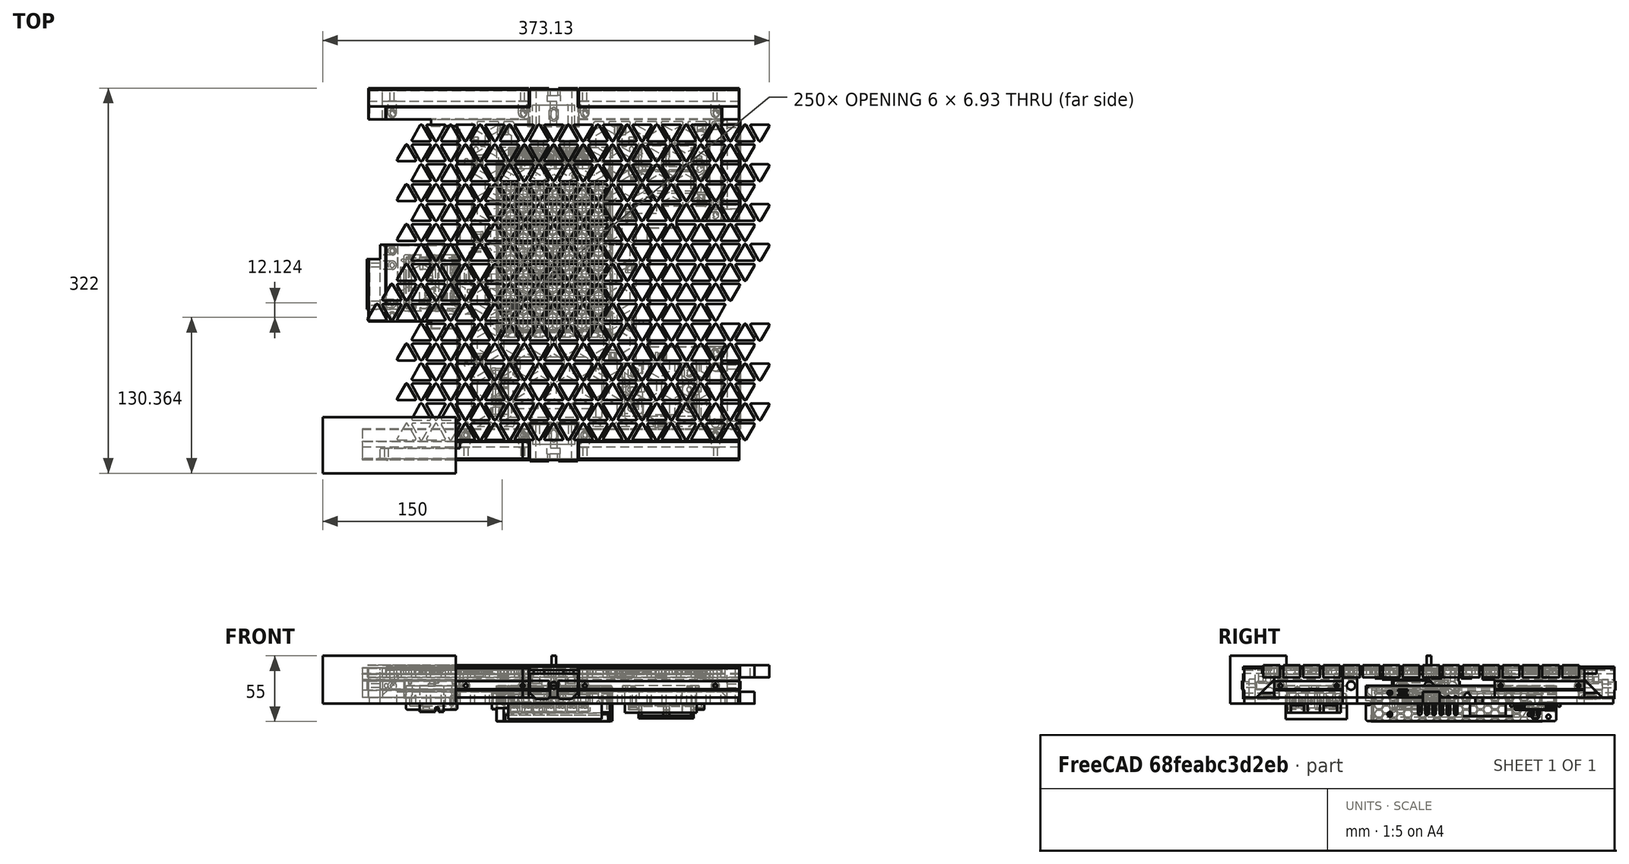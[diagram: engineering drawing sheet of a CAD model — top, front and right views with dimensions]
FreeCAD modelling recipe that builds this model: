
FCSTD DOCUMENT  (FreeCAD 0.19R24291 (Git))
Label: bottom-panel
License: Other
LicenseURL: GPL3
objects: Part::Feature×117, Part::Box×54, Part::MultiFuse×41, Part::Cut×29, Part::Cylinder×17, Part::Chamfer×14, Part::Fillet×5, Part::Extrusion×3, Mesh::Feature×1, Part::MultiCommon×1, Part::Refine×1
note: 282 computed .brp shape members not serialized (recipe doc carries the construction recipe); baked Part::Feature solids carry a one-line shape summary decoded from their .brp

FEATURE [Part::Box] Box  label="Cube"
  AttacherType = Attacher::AttachEngine3D
  Height = 3
  Length = 310
  Placement = pos=(-155,-155,28) rot=(0,0,1;0rad)
  Width = 310
FEATURE [Part::Box] Box002  label="Cube001"
  AttacherType = Attacher::AttachEngine3D
  Height = 10
  Length = 74.5
  Placement = pos=(80.5,-72,24) rot=(0,0,1;0rad)
  Width = 117
FEATURE [Part::Box] Box003  label="Cube002"
  AttacherType = Attacher::AttachEngine3D
  Height = 10
  Length = 74.5
  Placement = pos=(-155,-156,24) rot=(0,0,1;0rad)
  Width = 117
FEATURE [Part::Box] Box004  label="Cube003"
  AttacherType = Attacher::AttachEngine3D
  Height = 10
  Length = 74.5
  Placement = pos=(-155,13,24) rot=(0,0,1;0rad)
  Width = 117
FEATURE [Part::Box] Box005  label="Cube004"
  AttacherType = Attacher::AttachEngine3D
  Height = 3
  Length = 22
  Placement = pos=(-102.5,-45,28) rot=(0,0,1;0rad)
  Width = 6
FEATURE [Part::Box] Box006  label="Cube005"
  AttacherType = Attacher::AttachEngine3D
  Height = 3
  Length = 22
  Placement = pos=(80.5,39,28) rot=(0,0,1;0rad)
  Width = 6
FEATURE [Part::Box] Box007  label="Cube006"
  AttacherType = Attacher::AttachEngine3D
  Height = 3
  Length = 22
  Placement = pos=(-102.5,124,28) rot=(0,0,1;0rad)
  Width = 6
FEATURE [Part::Box] Box008  label="Cube007"
  AttacherType = Attacher::AttachEngine3D
  Height = 3
  Length = 64.5
  Placement = pos=(-145,-155,28) rot=(0,0,1;0rad)
  Width = 10
FEATURE [Part::Box] Box009  label="Cube008"
  AttacherType = Attacher::AttachEngine3D
  Height = 3
  Length = 64.5
  Placement = pos=(80.5,-72,28) rot=(0,0,1;0rad)
  Width = 12
FEATURE [Part::Box] Box010  label="Cube009"
  AttacherType = Attacher::AttachEngine3D
  Height = 3
  Length = 64.5
  Placement = pos=(-145,13,28) rot=(0,0,1;0rad)
  Width = 12
FEATURE [Part::Feature] Fusion006002011004053036004001028003005003001_cs001  label="base-plate-profile001"
  Placement = pos=(0,0,-29.5) rot=(0,0,1;0rad)
  shape: bbox 308 x 308 x 4e-07 mm, 0 faces, 0 solids (baked)
FEATURE [Part::Extrusion] Extrude
  Base = -> Fusion006002011004053036004001028003005003001_cs001
  Dir = (0,0,1)
  DirMode = 2
  FaceMakerClass = Part::FaceMakerBullseye
  LengthFwd = 5
  LengthRev = 0
  Placement = pos=(0,-185,0) rot=(0,0,1;0rad)
  Solid = true
  Symmetric = false
FEATURE [Mesh::Feature] _pospos  label=" pospos"
  Placement = pos=(0,-185,0) rot=(0,0,1;0rad)
FEATURE [Part::MultiFuse] Fusion
  Shapes = -> [Box002,Box004,Box003]
FEATURE [Part::Cut] Cut
  Base = -> Box
  Tool = -> Fusion
FEATURE [Part::Box] Box011  label="Cube010"
  AttacherType = Attacher::AttachEngine3D
  Height = 25
  Length = 10
  Placement = pos=(0,0,5) rot=(0,0,1;0rad)
  Width = 25
FEATURE [Part::Box] Box012  label="Cube011"
  AttacherType = Attacher::AttachEngine3D
  Height = 7.8
  Length = 10
  Placement = pos=(0,24,11.1) rot=(0,0,1;0rad)
  Width = 2
FEATURE [Part::Box] Box013  label="Cube012"
  AttacherType = Attacher::AttachEngine3D
  Height = 25
  Length = 10
  Placement = pos=(0,-14.75,25) rot=(0,0,1;0rad)
  Width = 25
FEATURE [Part::Cut] Cut001
  Base = -> Box011
  Tool = -> Box013
FEATURE [Part::Chamfer] Chamfer
  Base = -> Cut001
  Edges = 1 edges r=15: [Edge9]
FEATURE [Part::Chamfer] Chamfer001
  Base = -> Chamfer
  Edges = 3 edges r=0.4: [Edge10,Edge18,Edge20]
FEATURE [Part::MultiFuse] Fusion001002  label="support-profile"
  Shapes = -> [Chamfer001,Box012]
FEATURE [Part::MultiFuse] Fusion001003
  Shapes = -> [Box010,Box009,Box008,Box007,Box006,Box005,Cut]
FEATURE [Part::Feature] Fusion001002_cs  label="support-profile-template"
  shape: bbox 3e-07 x 26 x 25 mm, 0 faces, 0 solids (baked)
FEATURE [Part::Feature] Fusion001002_cs001  label="support-profile-template001"
  shape: bbox 3e-07 x 26 x 25 mm, 0 faces, 0 solids (baked)
FEATURE [Part::Extrusion] Extrude001  label="134mm0length"
  Base = -> Fusion001002_cs001
  Dir = (1,0,0)
  DirMode = 2
  FaceMakerClass = Part::FaceMakerBullseye
  LengthFwd = 134
  LengthRev = 0
  Placement = pos=(-21,-129,0) rot=(0,0,1;3.14159rad)
  Solid = true
  Symmetric = false
FEATURE [Part::Feature] Extrude001001  label="134mm0length001"
  Placement = pos=(-21,-129,0) rot=(0,0,1;3.14159rad)
  shape: bbox 134 x 26 x 25 mm, 16 faces (baked)
FEATURE [Part::Feature] Extrude001002  label="134mm0length002"
  Placement = pos=(160,-129,0) rot=(0,0,1;3.14159rad)
  shape: bbox 134 x 26 x 25 mm, 16 faces (baked)
FEATURE [Part::Feature] Extrude001003  label="134mm0length003"
  Placement = pos=(-160,130,0) rot=(0,0,1;0rad)
  shape: bbox 134 x 26 x 25 mm, 16 faces (baked)
FEATURE [Part::Feature] Extrude001004  label="134mm0length004"
  Placement = pos=(16,130,0) rot=(0,0,1;0rad)
  shape: bbox 134 x 26 x 25 mm, 16 faces (baked)
FEATURE [Part::Feature] Extrude001005  label="134mm0length005"
  Placement = pos=(-130,-61,0) rot=(0,0,1;1.5708rad)
  shape: bbox 26 x 134 x 25 mm, 16 faces (baked)
FEATURE [Part::Feature] Extrude001006  label="134mm0length006"
  Placement = pos=(130,-19,0) rot=(0,0,-1;1.5708rad)
  shape: bbox 26 x 134 x 25 mm, 16 faces (baked)
FEATURE [Part::Feature] Extrude001007  label="134mm0length007"
  Placement = pos=(130,167,0) rot=(0,0,-1;1.5708rad)
  shape: bbox 26 x 134 x 25 mm, 16 faces (baked)
FEATURE [Part::Box] Box014  label="Cube013"
  AttacherType = Attacher::AttachEngine3D
  Height = 40
  Length = 111
  Placement = pos=(-193,-166,0) rot=(0,0,1;0rad)
  Width = 47
FEATURE [Part::Box] Box015  label="Cube014"
  AttacherType = Attacher::AttachEngine3D
  Height = 40
  Length = 111
  Placement = pos=(-191.5,-145,0) rot=(0,0,1;0rad)
  Width = 47
FEATURE [Part::Box] Box016  label="Cube015"
  AttacherType = Attacher::AttachEngine3D
  Height = 40
  Length = 111
  Placement = pos=(-256,-178.5,0) rot=(0,0,1;0rad)
  Width = 47
FEATURE [Part::MultiFuse] Fusion001004
  Shapes = -> [Box016,Box015]
FEATURE [Part::Cut] Cut002
  Base = -> Extrude001001
  Tool = -> Fusion001004
FEATURE [Part::Box] Box017  label="Cube016"
  AttacherType = Attacher::AttachEngine3D
  Height = 40
  Length = 111
  Placement = pos=(-193,-86,0) rot=(0,0,1;0rad)
  Width = 47
FEATURE [Part::Box] Box018  label="Cube017"
  AttacherType = Attacher::AttachEngine3D
  Height = 40
  Length = 111
  Placement = pos=(-193,25,0) rot=(0,0,1;0rad)
  Width = 59
FEATURE [Part::Box] Box019  label="Cube018"
  AttacherType = Attacher::AttachEngine3D
  Height = 40
  Length = 111
  Placement = pos=(-256,13,0) rot=(0,0,1;0rad)
  Width = 59
FEATURE [Part::MultiFuse] Fusion001005
  Shapes = -> [Box019,Box018,Box017]
FEATURE [Part::Cut] Cut003
  Base = -> Extrude001005
  Tool = -> Fusion001005
FEATURE [Part::Box] Box020  label="Cube019"
  AttacherType = Attacher::AttachEngine3D
  Height = 40
  Length = 111
  Placement = pos=(117.5,-2,0) rot=(0,0,1;0rad)
  Width = 47
FEATURE [Part::Box] Box021  label="Cube020"
  AttacherType = Attacher::AttachEngine3D
  Height = 40
  Length = 111
  Placement = pos=(117.5,130,0) rot=(0,0,1;0rad)
  Width = 47
FEATURE [Part::MultiFuse] Fusion001006
  Shapes = -> [Box021,Box020]
FEATURE [Part::Cut] Cut004
  Base = -> Extrude001007
  Tool = -> Fusion001006
FEATURE [Part::Box] Box022  label="Cube021"
  AttacherType = Attacher::AttachEngine3D
  Height = 40
  Length = 111
  Placement = pos=(124.5,-176,0) rot=(0,0,1;0rad)
  Width = 47
FEATURE [Part::Box] Box023  label="Cube022"
  AttacherType = Attacher::AttachEngine3D
  Height = 40
  Length = 111
  Placement = pos=(124.5,-60,0) rot=(0,0,1;0rad)
  Width = 47
FEATURE [Part::Box] Box024  label="Cube023"
  AttacherType = Attacher::AttachEngine3D
  Height = 40
  Length = 111
  Placement = pos=(145,-72,0) rot=(0,0,1;0rad)
  Width = 47
FEATURE [Part::MultiFuse] Fusion001007
  Shapes = -> [Box022,Box024,Box023]
FEATURE [Part::Cut] Cut005
  Base = -> Extrude001006
  Tool = -> Fusion001007
FEATURE [Part::Box] Box025  label="Cube024"
  AttacherType = Attacher::AttachEngine3D
  Height = 6
  Length = 14.75
  Placement = pos=(-155,130,24) rot=(0,0,1;0rad)
  Width = 12
FEATURE [Part::Box] Box026  label="Cube025"
  AttacherType = Attacher::AttachEngine3D
  Height = 6
  Length = 14.75
  Placement = pos=(140.25,130,24) rot=(0,0,1;0rad)
  Width = 11
FEATURE [Part::Box] Box027  label="Cube026"
  AttacherType = Attacher::AttachEngine3D
  Height = 6
  Length = 14.75
  Placement = pos=(140.25,-140,24) rot=(0,0,1;0rad)
  Width = 11
FEATURE [Part::Feature] Defeatured001
  shape: bbox 134 x 26 x 25 mm, 14 faces (baked)
FEATURE [Part::Feature] Defeatured003
  shape: bbox 134 x 26 x 25 mm, 14 faces (baked)
FEATURE [Part::Feature] Defeatured005
  shape: bbox 134 x 26 x 25 mm, 14 faces (baked)
FEATURE [Part::MultiFuse] Fusion001008
  Shapes = -> [Box027,Defeatured005]
FEATURE [Part::MultiFuse] Fusion001009
  Shapes = -> [Defeatured003,Box026]
FEATURE [Part::MultiFuse] Fusion001010
  Shapes = -> [Defeatured001,Box025]
FEATURE [Part::Feature] Fusion001010001  label="Fusion001011"
  shape: bbox 134 x 26 x 25 mm, 15 faces (baked)
FEATURE [Part::Feature] Fusion001009001  label="Fusion001012"
  shape: bbox 134 x 26 x 25 mm, 15 faces (baked)
FEATURE [Part::Feature] Fusion001008001  label="Fusion001013"
  shape: bbox 134 x 26 x 25 mm, 15 faces (baked)
FEATURE [Part::Chamfer] Chamfer002
  Base = -> Fusion001010001
  Edges = 4 edges r=0.4: [Edge9,Edge32,Edge35,Edge37]
FEATURE [Part::Chamfer] Chamfer003
  Base = -> Fusion001009001
  Edges = 4 edges r=0.4: [Edge19,Edge21,Edge24,Edge39]
FEATURE [Part::Chamfer] Chamfer004
  Base = -> Fusion001008001
  Edges = 4 edges r=0.4: [Edge2,Edge16,Edge19,Edge38]
FEATURE [Part::Cylinder] Cylinder
  Angle = 360
  AttacherType = Attacher::AttachEngine3D
  Height = 20
  Placement = pos=(10,0,15) rot=(0,-1,0;1.5708rad)
  Radius = 3.5
FEATURE [Part::Cylinder] Cylinder001
  Angle = 360
  AttacherType = Attacher::AttachEngine3D
  Height = 11
  Placement = pos=(-10,0,15) rot=(0,-1,0;1.5708rad)
  Radius = 1.65
FEATURE [Part::Cylinder] Cylinder002
  Angle = 360
  AttacherType = Attacher::AttachEngine3D
  Height = 40
  Radius = 1.9
FEATURE [Part::MultiFuse] Fusion001010002  label="bolt-slot"
  Shapes = -> [Cylinder002,Cylinder001,Cylinder]
FEATURE [Part::Feature] Fusion001010002001  label="bolt-slot001"
  shape: bbox 31 x 7 x 40 mm, 9 faces (baked)
FEATURE [Part::Feature] Fusion001010002002  label="bolt-slot002"
  Placement = pos=(-135,8,0) rot=(0,0,1;0rad)
  shape: bbox 31 x 7 x 40 mm, 9 faces (baked)
FEATURE [Part::Feature] Fusion001010002003  label="bolt-slot003"
  Placement = pos=(-135,-34,0) rot=(0,0,1;0rad)
  shape: bbox 31 x 7 x 40 mm, 9 faces (baked)
FEATURE [Part::Feature] Fusion001010002005  label="bolt-slot004"
  Placement = pos=(-26,135,0) rot=(0,0,-1;1.5708rad)
  shape: bbox 7 x 31 x 40 mm, 9 faces (baked)
FEATURE [Part::Feature] Fusion001010002006  label="bolt-slot005"
  Placement = pos=(-135,135,0) rot=(0,0,-1;1.5708rad)
  shape: bbox 7 x 31 x 40 mm, 9 faces (baked)
FEATURE [Part::Feature] Fusion001010002007  label="bolt-slot006"
  Placement = pos=(26,135,0) rot=(0,0,-1;1.5708rad)
  shape: bbox 7 x 31 x 40 mm, 9 faces (baked)
FEATURE [Part::Feature] Fusion001010002008  label="bolt-slot007"
  Placement = pos=(135,135,0) rot=(0,0,-1;1.5708rad)
  shape: bbox 7 x 31 x 40 mm, 9 faces (baked)
FEATURE [Part::Feature] Fusion001010002009  label="bolt-slot008"
  Placement = pos=(135,125,0) rot=(0,0,1;3.14159rad)
  shape: bbox 31 x 7 x 40 mm, 9 faces (baked)
FEATURE [Part::Feature] Fusion001010002010  label="bolt-slot009"
  Placement = pos=(135,50,0) rot=(0,0,1;3.14159rad)
  shape: bbox 31 x 7 x 40 mm, 9 faces (baked)
FEATURE [Part::Feature] Fusion001010002011  label="bolt-slot010"
  Placement = pos=(135,-65,0) rot=(0,0,1;3.14159rad)
  shape: bbox 31 x 7 x 40 mm, 9 faces (baked)
FEATURE [Part::Feature] Fusion001010002012  label="bolt-slot011"
  Placement = pos=(135,-124,0) rot=(0,0,1;3.14159rad)
  shape: bbox 31 x 7 x 40 mm, 9 faces (baked)
FEATURE [Part::Feature] Fusion001010002013  label="bolt-slot012"
  Placement = pos=(135,-134,0) rot=(0,0,1;1.5708rad)
  shape: bbox 7 x 31 x 40 mm, 9 faces (baked)
FEATURE [Part::Feature] Fusion001010002014  label="bolt-slot013"
  Placement = pos=(26,-134,0) rot=(0,0,1;1.5708rad)
  shape: bbox 7 x 31 x 40 mm, 9 faces (baked)
FEATURE [Part::Feature] Fusion001010002015  label="bolt-slot014"
  Placement = pos=(-26,-134,0) rot=(0,0,1;1.5708rad)
  shape: bbox 7 x 31 x 40 mm, 9 faces (baked)
FEATURE [Part::Feature] Fusion001010002016  label="bolt-slot015"
  Placement = pos=(-73.5,-134,0) rot=(0,0,1;1.5708rad)
  shape: bbox 7 x 31 x 40 mm, 9 faces (baked)
FEATURE [Part::Feature] Fusion001010002017  label="bolt-slot016"
  Placement = pos=(-140,-134,0) rot=(0,0,1;1.5708rad)
  shape: bbox 7 x 31 x 40 mm, 9 faces (baked)
FEATURE [Part::Box] Box028  label="Cube027"
  AttacherType = Attacher::AttachEngine3D
  Height = 40
  Length = 330
  Placement = pos=(-165,140,0) rot=(0,0,1;0rad)
  Width = 20
FEATURE [Part::Box] Box029  label="Cube028"
  AttacherType = Attacher::AttachEngine3D
  Height = 40
  Length = 330
  Placement = pos=(-165,-159,0) rot=(0,0,1;0rad)
  Width = 20
FEATURE [Part::Box] Box030  label="Cube029"
  AttacherType = Attacher::AttachEngine3D
  Height = 40
  Length = 30
  Placement = pos=(-170,-170,0) rot=(0,0,1;0rad)
  Width = 330
FEATURE [Part::Box] Box031  label="Cube030"
  AttacherType = Attacher::AttachEngine3D
  Height = 40
  Length = 30
  Placement = pos=(140,-170,0) rot=(0,0,1;0rad)
  Width = 330
FEATURE [Part::Box] Box032  label="Cube031"
  AttacherType = Attacher::AttachEngine3D
  Height = 40
  Length = 40
  Placement = pos=(-20,140,0) rot=(0,0,1;0rad)
  Width = 17
FEATURE [Part::Box] Box033  label="Cube032"
  AttacherType = Attacher::AttachEngine3D
  Height = 40
  Length = 40
  Placement = pos=(-20,-156,0) rot=(0,0,1;0rad)
  Width = 17
FEATURE [Part::MultiFuse] Fusion001010002020
  Shapes = -> [Box033,Box032]
FEATURE [Part::MultiFuse] Fusion001010002021
  Shapes = -> [Box028,Box029,Box030,Box031]
FEATURE [Part::Cut] Cut007
  Base = -> Fusion001010002021
  Tool = -> Fusion001010002020
FEATURE [Part::Cut] Cut008
  Base = -> Fusion001003
  Tool = -> Cut007
FEATURE [Part::Feature] Cut002001  label="Cut009"
  Placement = pos=(5,0,0) rot=(0,0,1;0rad)
  shape: bbox 119 x 26 x 25 mm, 18 faces (baked)
FEATURE [Part::Feature] Fusion001010002023  label="bolt-slot017"
  Placement = pos=(135,-77,0) rot=(0,0,1;3.14159rad)
  shape: bbox 31 x 7 x 40 mm, 9 faces (baked)
FEATURE [Part::Feature] Fusion001010002024  label="bolt-slot018"
  Placement = pos=(-135,20,0) rot=(0,0,1;0rad)
  shape: bbox 31 x 7 x 40 mm, 9 faces (baked)
FEATURE [Part::MultiFuse] Fusion001010002026
  Shapes = -> [Fusion001010002006,Fusion001010002005]
FEATURE [Part::Cut] Cut002003
  Base = -> Chamfer002
  Tool = -> Fusion001010002026
FEATURE [Part::MultiFuse] Fusion001010002027
  Shapes = -> [Fusion001010002008,Fusion001010002007]
FEATURE [Part::Cut] Cut002004  label="panel-mount-BR"
  Base = -> Chamfer003
  Tool = -> Fusion001010002027
FEATURE [Part::MultiFuse] Fusion001010002029
  Shapes = -> [Fusion001010002012,Fusion001010002023,Fusion001010002011]
FEATURE [Part::Cut] Cut002006  label="panel-mount-FMR"
  Base = -> Cut005
  Tool = -> Fusion001010002029
FEATURE [Part::Feature] Cut008001_cs
  shape: bbox 280 x 310 x 3e-07 mm, 0 faces, 0 solids (baked)
FEATURE [Part::Extrusion] Extrude001008
  Base = -> Cut008001_cs
  Dir = (0,0,1)
  DirMode = 2
  FaceMakerClass = Part::FaceMakerBullseye
  LengthFwd = 5
  LengthRev = 0
  Placement = pos=(0,0,-5) rot=(0,0,1;0rad)
  Solid = true
  Symmetric = false
FEATURE [Part::Feature] Fusion001010002032002  label="Fusion001010002034"
  Placement = pos=(-26,135,0) rot=(0,0,1;0rad)
  shape: bbox 6 x 6 x 35 mm, 7 faces (baked)
FEATURE [Part::Feature] Fusion001010002032003  label="Fusion001010002035"
  Placement = pos=(26,135,0) rot=(0,0,1;0rad)
  shape: bbox 6 x 6 x 35 mm, 7 faces (baked)
FEATURE [Part::Feature] Fusion001010002032004  label="Fusion001010002036"
  Placement = pos=(135,135,0) rot=(0,0,1;0rad)
  shape: bbox 6 x 6 x 35 mm, 7 faces (baked)
FEATURE [Part::Feature] Fusion001010002032005  label="Fusion001010002037"
  Placement = pos=(135,50,0) rot=(0,0,1;0rad)
  shape: bbox 6 x 6 x 35 mm, 7 faces (baked)
FEATURE [Part::Feature] Fusion001010002032006  label="Fusion001010002038"
  Placement = pos=(135,-65,0) rot=(0,0,1;0rad)
  shape: bbox 6 x 6 x 35 mm, 7 faces (baked)
FEATURE [Part::Feature] Fusion001010002032007  label="Fusion001010002039"
  Placement = pos=(135,-134,0) rot=(0,0,1;0rad)
  shape: bbox 6 x 6 x 35 mm, 7 faces (baked)
FEATURE [Part::Feature] Fusion001010002032008  label="Fusion001010002040"
  Placement = pos=(-26,-134,0) rot=(0,0,1;0rad)
  shape: bbox 6 x 6 x 35 mm, 7 faces (baked)
FEATURE [Part::Feature] Fusion001010002032009  label="Fusion001010002041"
  Placement = pos=(-73.5,-134,0) rot=(0,0,1;0rad)
  shape: bbox 6 x 6 x 35 mm, 7 faces (baked)
FEATURE [Part::Feature] Fusion001010002032010  label="Fusion001010002042"
  Placement = pos=(-135,-34,0) rot=(0,0,1;0rad)
  shape: bbox 6 x 6 x 35 mm, 7 faces (baked)
FEATURE [Part::Feature] Fusion001010002032011  label="Fusion001010002043"
  Placement = pos=(-135,20,0) rot=(0,0,1;0rad)
  shape: bbox 6 x 6 x 35 mm, 7 faces (baked)
FEATURE [Part::Feature] Fusion001010002032012  label="Fusion001010002044"
  Placement = pos=(-135,135,0) rot=(0,0,1;0rad)
  shape: bbox 6 x 6 x 35 mm, 7 faces (baked)
FEATURE [Part::Feature] Fusion001010002032014
  Placement = pos=(26,-134,0) rot=(0,0,1;0rad)
  shape: bbox 6 x 6 x 35 mm, 7 faces (baked)
FEATURE [Part::Feature] Chamfer003001  label="din-end"
  Placement = pos=(0,140,0) rot=(0,0,1;0rad)
  shape: bbox 40 x 31 x 21 mm, 75 faces (baked)
FEATURE [Part::Feature] Chamfer003002  label="din-end001"
  Placement = pos=(-7.8e-14,-140,0) rot=(0,0,1;3.14159rad)
  shape: bbox 40 x 31 x 21 mm, 75 faces (baked)
FEATURE [Part::Box] Box034  label="Cube033"
  AttacherType = Attacher::AttachEngine3D
  Height = 40
  Length = 42
  Placement = pos=(-21,124,0) rot=(0,0,1;0rad)
  Width = 31
FEATURE [Part::Box] Box035  label="Cube034"
  AttacherType = Attacher::AttachEngine3D
  Height = 40
  Length = 42
  Placement = pos=(-21,-155,0) rot=(0,0,1;0rad)
  Width = 31
FEATURE [Part::MultiFuse] Fusion001010002032016
  Shapes = -> [Box035,Box034]
FEATURE [Part::Feature] Fusion001010002032017001  label="Fusion001010002032018"
  shape: bbox 280 x 279 x 10 mm, 54 faces (baked)
FEATURE [Part::Fillet] Fillet  label="outer-cut"
  Base = -> Fusion001010002032017001
  Edges = 23 edges r=2: [Edge92,Edge93,Edge95,Edge97,Edge98,Edge100,Edge101,Edge103,Edge105,Edge107,Edge108,Edge110,Edge111,Edge113,Edge117,Edge118,Edge120,Edge121,Edge123,Edge124,Edge125,Edge127,Edge129]
  Placement = pos=(0,0,-1.5) rot=(0,0,1;0rad)
FEATURE [Part::Feature] Fillet001001  label="Fillet002"
  shape: bbox 15.86 x 14 x 10 mm, 8 faces (baked)
FEATURE [Part::Feature] Fillet001002  label="Fillet003"
  Placement = pos=(12.3,4,0) rot=(0,0,1;3.14159rad)
  shape: bbox 15.86 x 14 x 10 mm, 8 faces (baked)
FEATURE [Part::Feature] Fillet001003  label="Fillet004"
  Placement = pos=(24.6,0,0) rot=(0,0,1;0rad)
  shape: bbox 15.86 x 14 x 10 mm, 8 faces (baked)
FEATURE [Part::Feature] Fillet001004  label="Fillet005"
  Placement = pos=(36.9,4,0) rot=(0,0,1;3.14159rad)
  shape: bbox 15.86 x 14 x 10 mm, 8 faces (baked)
FEATURE [Part::Feature] Fillet001005  label="Fillet006"
  Placement = pos=(61.5,4,0) rot=(0,0,1;3.14159rad)
  shape: bbox 15.86 x 14 x 10 mm, 8 faces (baked)
FEATURE [Part::Feature] Fillet001006  label="Fillet007"
  Placement = pos=(86.1,4,0) rot=(0,0,1;3.14159rad)
  shape: bbox 15.86 x 14 x 10 mm, 8 faces (baked)
FEATURE [Part::Feature] Fillet001007  label="Fillet008"
  Placement = pos=(110.7,4,0) rot=(0,0,1;3.14159rad)
  shape: bbox 15.86 x 14 x 10 mm, 8 faces (baked)
FEATURE [Part::Feature] Fillet001008  label="Fillet009"
  Placement = pos=(135.3,4,0) rot=(0,0,1;3.14159rad)
  shape: bbox 15.86 x 14 x 10 mm, 8 faces (baked)
FEATURE [Part::Feature] Fillet001009  label="Fillet010"
  Placement = pos=(159.9,4,0) rot=(0,0,1;3.14159rad)
  shape: bbox 15.86 x 14 x 10 mm, 8 faces (baked)
FEATURE [Part::Feature] Fillet001010  label="Fillet011"
  Placement = pos=(49.2,0,0) rot=(0,0,1;0rad)
  shape: bbox 15.86 x 14 x 10 mm, 8 faces (baked)
FEATURE [Part::Feature] Fillet001011  label="Fillet012"
  Placement = pos=(73.8,0,0) rot=(0,0,1;0rad)
  shape: bbox 15.86 x 14 x 10 mm, 8 faces (baked)
FEATURE [Part::Feature] Fillet001012  label="Fillet013"
  Placement = pos=(98.4,0,0) rot=(0,0,1;0rad)
  shape: bbox 15.86 x 14 x 10 mm, 8 faces (baked)
FEATURE [Part::Feature] Fillet001013  label="Fillet014"
  Placement = pos=(123,0,0) rot=(0,0,1;0rad)
  shape: bbox 15.86 x 14 x 10 mm, 8 faces (baked)
FEATURE [Part::Feature] Fillet001014  label="Fillet015"
  Placement = pos=(147.6,0,0) rot=(0,0,1;0rad)
  shape: bbox 15.86 x 14 x 10 mm, 8 faces (baked)
FEATURE [Part::Feature] Fillet001015  label="Fillet016"
  Placement = pos=(-24.6,0,0) rot=(0,0,1;0rad)
  shape: bbox 15.86 x 14 x 10 mm, 8 faces (baked)
FEATURE [Part::Feature] Fillet001016  label="Fillet017"
  Placement = pos=(-49.2,0,0) rot=(0,0,1;0rad)
  shape: bbox 15.86 x 14 x 10 mm, 8 faces (baked)
FEATURE [Part::Feature] Fillet001017  label="Fillet018"
  Placement = pos=(-73.8,0,0) rot=(0,0,1;0rad)
  shape: bbox 15.86 x 14 x 10 mm, 8 faces (baked)
FEATURE [Part::Feature] Fillet001018  label="Fillet019"
  Placement = pos=(-98.4,0,0) rot=(0,0,1;0rad)
  shape: bbox 15.86 x 14 x 10 mm, 8 faces (baked)
FEATURE [Part::Feature] Fillet001019  label="Fillet020"
  Placement = pos=(-123,0,0) rot=(0,0,1;0rad)
  shape: bbox 15.86 x 14 x 10 mm, 8 faces (baked)
FEATURE [Part::Feature] Fillet001020  label="Fillet021"
  Placement = pos=(-12.3,4,0) rot=(0,0,1;3.14159rad)
  shape: bbox 15.86 x 14 x 10 mm, 8 faces (baked)
FEATURE [Part::Feature] Fillet001021  label="Fillet022"
  Placement = pos=(-36.9,4,0) rot=(0,0,1;3.14159rad)
  shape: bbox 15.86 x 14 x 10 mm, 8 faces (baked)
FEATURE [Part::Feature] Fillet001022  label="Fillet023"
  Placement = pos=(-61.5,4,0) rot=(0,0,1;3.14159rad)
  shape: bbox 15.86 x 14 x 10 mm, 8 faces (baked)
FEATURE [Part::Feature] Fillet001023  label="Fillet024"
  Placement = pos=(-86.1,4,0) rot=(0,0,1;3.14159rad)
  shape: bbox 15.86 x 14 x 10 mm, 8 faces (baked)
FEATURE [Part::Feature] Fillet001024  label="Fillet025"
  Placement = pos=(-110.7,4,0) rot=(0,0,1;3.14159rad)
  shape: bbox 15.86 x 14 x 10 mm, 8 faces (baked)
FEATURE [Part::MultiFuse] Fusion001010002032017002
  Shapes = -> [Fillet001024,Fillet001017,Fillet001002,Fillet001004,Fillet001011,Fillet001005,Fillet001009,Fillet001006,Fillet001014,Fillet001015,Fillet001008,Fillet001010,Fillet001003,Fillet001016,Fillet001020,Fillet001021,Fillet001023,Fillet001007,Fillet001001,Fillet001012,Fillet001022,Fillet001013,Fillet001018,Fillet001019]
FEATURE [Part::Feature] Fusion001010002032017002003001  label="Fusion001010002032017002004"
  shape: bbox 311.1 x 30.65 x 10 mm, 384 faces, 48 solids (baked)
FEATURE [Part::Feature] Fusion001010002032017002003002  label="Fusion001010002032017002005"
  Placement = pos=(0,33.3,0) rot=(0,0,1;0rad)
  shape: bbox 311.1 x 30.65 x 10 mm, 384 faces, 48 solids (baked)
FEATURE [Part::Feature] Fusion001010002032017002003003  label="Fusion001010002032017002006"
  Placement = pos=(-24.6,-33.3,0) rot=(0,0,1;0rad)
  shape: bbox 311.1 x 30.65 x 10 mm, 384 faces, 48 solids (baked)
FEATURE [Part::Feature] Fusion001010002032017002003004  label="Fusion001010002032017002007"
  Placement = pos=(0,-66.6,0) rot=(0,0,1;0rad)
  shape: bbox 311.1 x 30.65 x 10 mm, 384 faces, 48 solids (baked)
FEATURE [Part::Feature] Fusion001010002032017002003005  label="Fusion001010002032017002008"
  Placement = pos=(0,-99.9,0) rot=(0,0,1;0rad)
  shape: bbox 311.1 x 30.65 x 10 mm, 384 faces, 48 solids (baked)
FEATURE [Part::Feature] Fusion001010002032017002003006  label="Fusion001010002032017002009"
  Placement = pos=(0,-133.2,0) rot=(0,0,1;0rad)
  shape: bbox 311.1 x 30.65 x 10 mm, 384 faces, 48 solids (baked)
FEATURE [Part::Feature] Fusion001010002032017002003007  label="Fusion001010002032017002010"
  Placement = pos=(0,66.6,0) rot=(0,0,1;0rad)
  shape: bbox 311.1 x 30.65 x 10 mm, 384 faces, 48 solids (baked)
FEATURE [Part::Feature] Fusion001010002032017002003008  label="Fusion001010002032017002011"
  Placement = pos=(0,99.9,0) rot=(0,0,1;0rad)
  shape: bbox 311.1 x 30.65 x 10 mm, 384 faces, 48 solids (baked)
FEATURE [Part::MultiFuse] Fusion001010002032017002003009
  Placement = pos=(0,0,22) rot=(0,0,1;0rad)
  Shapes = -> [Fusion001010002032017002003001,Fusion001010002032017002003008,Fusion001010002032017002003004,Fusion001010002032017002003003,Fusion001010002032017002003006,Fusion001010002032017002003005,Fusion001010002032017002003002,Fusion001010002032017002003007]
FEATURE [Part::Feature] Extrude001008001  label="Extrude001009"
  Placement = pos=(0,0,-5) rot=(0,0,1;0rad)
  shape: bbox 280 x 310 x 5 mm, 30 faces (baked)
FEATURE [Part::Feature] Fusion001010002032016001  label="Fusion001010002032017002003010"
  shape: bbox 42 x 310 x 40 mm, 12 faces, 2 solids (baked)
FEATURE [Part::Cut] Cut002011
  Base = -> Extrude001008001
  Placement = pos=(0,0,-23) rot=(0,0,1;0rad)
  Tool = -> Fusion001010002032016001
FEATURE [Part::Feature] Fusion001018001  label="Fusion001019"
  shape: bbox 303.3 x 320 x 10 mm, 1832 faces, 229 solids (baked)
FEATURE [Part::MultiCommon] Common
  Shapes = -> [Fusion001018001,Cut002011]
FEATURE [Part::Cut] Cut002012
  Base = -> Common
  Placement = pos=(0,0,21.5) rot=(0,0,1;0rad)
  Tool = -> Fillet
FEATURE [Part::Cut] Cut002013
  Base = -> Extrude001008
  Tool = -> Fusion001010002032016
FEATURE [Part::Feature] Fusion006002011004053036004001028003005005  label="SSR"
  Placement = pos=(89,-96,-7) rot=(0.57735,-0.57735,0.57735;4.18879rad)
  shape: bbox 64 x 45 x 22.5 mm, 84 faces (baked)
FEATURE [Part::Feature] Fusion006002011004053036004001028003005006  label="RS-25-5-PSU"
  Placement = pos=(1,-94,15) rot=(-1,0,0;1.5708rad)
  shape: bbox 91.75 x 51 x 28 mm, 292 faces (baked)
FEATURE [Part::Feature] Fusion006002011004053036004001028003005004  label="SonOff-mini"
  Placement = pos=(-102,-7,5) rot=(0.57735,-0.57735,0.57735;4.18879rad)
  shape: bbox 43.4 x 42.65 x 19.85 mm, 152 faces (baked)
FEATURE [Part::Feature] Fusion006002011004053036004001028003005003  label="PSU-LRS-150-24"
  Placement = pos=(0.5,27,15) rot=(-1,0,0;1.5708rad)
  shape: bbox 97.2 x 159 x 30.02 mm, 3511 faces (baked)
FEATURE [Part::Feature] Chamfer005007002001  label="sonoff-top "
  Placement = pos=(-102,-7,14.5) rot=(0.707107,-0.707107,0;3.14159rad)
  shape: bbox 47 x 47 x 26.5 mm, 96 faces (baked)
FEATURE [Part::Feature] Cut002015002
  Placement = pos=(-102,6.5,27.5) rot=(0,1,0;3.14159rad)
  shape: bbox 20 x 20 x 3 mm, 23 faces (baked)
FEATURE [Part::Feature] Cut002015003
  Placement = pos=(-102,-20,27.5) rot=(0,1,0;3.14159rad)
  shape: bbox 20 x 20 x 3 mm, 23 faces (baked)
FEATURE [Part::Feature] Chamfer005007002002  label="sonoff-top 001"
  Placement = pos=(-102,-7,14.5) rot=(0.707107,-0.707107,0;3.14159rad)
  shape: bbox 47 x 47 x 26.5 mm, 96 faces (baked)
FEATURE [Part::Feature] Cut002015004
  Placement = pos=(113,-96,27.5) rot=(0,1,0;3.14159rad)
  shape: bbox 20 x 20 x 3 mm, 23 faces (baked)
FEATURE [Part::Feature] Cut002015005
  Placement = pos=(65.5,-96,27.5) rot=(0,1,0;3.14159rad)
  shape: bbox 20 x 20 x 3 mm, 23 faces (baked)
FEATURE [Part::Feature] Cut009001  label="wago-3x005"
  Placement = pos=(95,89,1.2e-14) rot=(0.707107,0.707107,0;3.14159rad)
  shape: bbox 63.6 x 41.99 x 12.2 mm, 224 faces (baked)
FEATURE [Part::Feature] Cut002015006
  Placement = pos=(121.5,89,27.5) rot=(0,1,0;3.14159rad)
  shape: bbox 20 x 20 x 3 mm, 23 faces (baked)
FEATURE [Part::Feature] Cut002015007
  Placement = pos=(66.5,89,27.5) rot=(0,1,0;3.14159rad)
  shape: bbox 20 x 20 x 3 mm, 23 faces (baked)
FEATURE [Part::Cylinder] Cylinder003
  Angle = 360
  AttacherType = Attacher::AttachEngine3D
  Height = 3.5
  Placement = pos=(66.5,89,24.5) rot=(0,0,1;0rad)
  Radius = 1.9
FEATURE [Part::Cylinder] Cylinder004
  Angle = 360
  AttacherType = Attacher::AttachEngine3D
  Height = 3.5
  Placement = pos=(121.5,89,24.5) rot=(0,0,1;0rad)
  Radius = 1.9
FEATURE [Part::Cylinder] Cylinder005
  Angle = 360
  AttacherType = Attacher::AttachEngine3D
  Height = 3.5
  Placement = pos=(113,-96,24.5) rot=(0,0,1;0rad)
  Radius = 1.9
FEATURE [Part::Cylinder] Cylinder006
  Angle = 360
  AttacherType = Attacher::AttachEngine3D
  Height = 3.5
  Placement = pos=(65.5,-96,24.5) rot=(0,0,1;0rad)
  Radius = 1.9
FEATURE [Part::Cylinder] Cylinder007
  Angle = 360
  AttacherType = Attacher::AttachEngine3D
  Height = 3.5
  Placement = pos=(-102,-20,24.5) rot=(0,0,1;0rad)
  Radius = 1.9
FEATURE [Part::Cylinder] Cylinder008
  Angle = 360
  AttacherType = Attacher::AttachEngine3D
  Height = 3.5
  Placement = pos=(-102,6.5,24.5) rot=(0,0,1;0rad)
  Radius = 1.9
FEATURE [Part::Feature] Chamfer001001  label="ziptie"
  Placement = pos=(94,-72,28) rot=(0,1,0;3.14159rad)
  shape: bbox 9 x 7 x 7 mm, 14 faces (baked)
FEATURE [Part::Feature] Chamfer005007002003  label="ziptie001"
  Placement = pos=(94,-128,28) rot=(0,1,0;3.14159rad)
  shape: bbox 9 x 7 x 7 mm, 14 faces (baked)
FEATURE [Part::Feature] Chamfer005007002005  label="ziptie003"
  Placement = pos=(-66,27,28) rot=(0.707107,0.707107,0;3.14159rad)
  shape: bbox 7 x 9 x 7 mm, 14 faces (baked)
FEATURE [Part::Feature] Chamfer005007002006  label="ziptie004"
  Placement = pos=(-66,91,28) rot=(0.707107,0.707107,0;3.14159rad)
  shape: bbox 7 x 9 x 7 mm, 14 faces (baked)
FEATURE [Part::Feature] Chamfer005007002008  label="ziptie006"
  Placement = pos=(60,-45,28) rot=(0.707107,0.707107,0;3.14159rad)
  shape: bbox 7 x 9 x 7 mm, 14 faces (baked)
FEATURE [Part::Feature] Chamfer005007002009  label="ziptie007"
  Placement = pos=(60,2,28) rot=(0.707107,0.707107,0;3.14159rad)
  shape: bbox 7 x 9 x 7 mm, 14 faces (baked)
FEATURE [Part::Feature] Chamfer005007002010  label="ziptie008"
  Placement = pos=(60,46,28) rot=(0.707107,0.707107,0;3.14159rad)
  shape: bbox 7 x 9 x 7 mm, 14 faces (baked)
FEATURE [Part::Feature] Chamfer005007002011  label="ziptie009"
  Placement = pos=(60,117,28) rot=(0,1,0;3.14159rad)
  shape: bbox 9 x 7 x 7 mm, 14 faces (baked)
FEATURE [Part::Feature] Chamfer005007002012  label="ziptie010"
  Placement = pos=(-38,117,28) rot=(0,1,0;3.14159rad)
  shape: bbox 9 x 7 x 7 mm, 14 faces (baked)
FEATURE [Part::Feature] Chamfer005007002013  label="ziptie011"
  Placement = pos=(46,-72,28) rot=(0.707107,0.707107,0;3.14159rad)
  shape: bbox 7 x 9 x 7 mm, 14 faces (baked)
FEATURE [Part::Feature] Chamfer005007002014  label="ziptie012"
  Placement = pos=(-66,-75,28) rot=(0.707107,0.707107,0;3.14159rad)
  shape: bbox 7 x 9 x 7 mm, 14 faces (baked)
FEATURE [Part::Feature] Chamfer005007002015  label="ziptie013"
  Placement = pos=(127,119,28) rot=(0,1,0;3.14159rad)
  shape: bbox 9 x 7 x 7 mm, 14 faces (baked)
FEATURE [Part::Feature] Chamfer005007002017  label="ziptie015"
  Placement = pos=(120,60,28) rot=(0.707107,0.707107,0;3.14159rad)
  shape: bbox 7 x 9 x 7 mm, 14 faces (baked)
FEATURE [Part::Box] Box036  label="Cube035"
  AttacherType = Attacher::AttachEngine3D
  Height = 20
  Length = 12
  Placement = pos=(-155,116,0) rot=(0,0,1;0rad)
  Width = 42
FEATURE [Part::Box] Box037  label="Cube036"
  AttacherType = Attacher::AttachEngine3D
  Height = 20
  Length = 42
  Placement = pos=(-166,-71,0) rot=(0,0,1;0rad)
  Width = 42
FEATURE [Part::Cut] Cut002015010  label="panel-mount-BL"
  Base = -> Cut002003
  Tool = -> Box036
FEATURE [Part::MultiFuse] Fusion006002011004053036004001028003005014002
  Shapes = -> [Fusion001010002013,Fusion001010002014]
FEATURE [Part::Cut] Cut002015011  label="panel-mount-FR"
  Base = -> Chamfer004
  Tool = -> Fusion006002011004053036004001028003005014002
FEATURE [Part::Feature] Fusion006002011004053036004001028003005014003  label="bolt-slot019"
  Placement = pos=(-135,-24,0) rot=(0,0,1;0rad)
  shape: bbox 31 x 7 x 40 mm, 9 faces (baked)
FEATURE [Part::MultiFuse] Fusion006002011004053036004001028003005014004
  Shapes = -> [Fusion006002011004053036004001028003005014003,Fusion001010002024,Fusion001010002002,Fusion001010002003]
FEATURE [Part::Cut] Cut002015012
  Base = -> Cut003
  Tool = -> Fusion006002011004053036004001028003005014004
FEATURE [Part::Cut] Cut002015013  label="panel-mount-ML"
  Base = -> Cut002015012
  Tool = -> Box037
FEATURE [Part::Box] Box038  label="Cube037"
  AttacherType = Attacher::AttachEngine3D
  Height = 20
  Length = 42
  Placement = pos=(124,13,0) rot=(0,0,1;0rad)
  Width = 42
FEATURE [Part::Feature] Fusion006002011004053036004001028003005014005  label="bolt-slot020"
  Placement = pos=(135,60,0) rot=(0,0,1;3.14159rad)
  shape: bbox 31 x 7 x 40 mm, 9 faces (baked)
FEATURE [Part::MultiFuse] Fusion006002011004053036004001028003005014006
  Shapes = -> [Fusion006002011004053036004001028003005014005,Fusion001010002009,Fusion001010002010]
FEATURE [Part::Cut] Cut002015014
  Base = -> Cut004
  Tool = -> Fusion006002011004053036004001028003005014006
FEATURE [Part::Cut] Cut002015015  label="panel-mount-BMR"
  Base = -> Cut002015014
  Tool = -> Box038
FEATURE [Part::Box] Box039  label="Cube038"
  AttacherType = Attacher::AttachEngine3D
  Height = 5
  Length = 21
  Placement = pos=(-73,-48,24.5) rot=(0,0,1;0rad)
  Width = 31
FEATURE [Part::Box] Box040  label="Cube039"
  AttacherType = Attacher::AttachEngine3D
  Height = 9
  Length = 15
  Placement = pos=(-70,-45,24.5) rot=(0,0,1;0rad)
  Width = 25
FEATURE [Part::Fillet] Fillet001025
  Base = -> Box040
  Edges = 4 edges r=2: [Edge1,Edge3,Edge5,Edge7]
  Placement = pos=(0,39,0) rot=(0,0,1;0rad)
FEATURE [Part::Box] Box041  label="Cube040"
  AttacherType = Attacher::AttachEngine3D
  Height = 5
  Length = 15
  Placement = pos=(-70,-45,24.5) rot=(0,0,1;0rad)
  Width = 25
FEATURE [Part::Fillet] Fillet001026
  Base = -> Box039
  Edges = 4 edges r=2: [Edge1,Edge3,Edge5,Edge7]
FEATURE [Part::Fillet] Fillet001027
  Base = -> Box041
  Edges = 4 edges r=2: [Edge1,Edge3,Edge5,Edge7]
FEATURE [Part::Cut] Cut002015017
  Base = -> Fillet001026
  Placement = pos=(0,39,0) rot=(0,0,1;0rad)
  Tool = -> Fillet001027
FEATURE [Part::Box] Box046  label="Cube045"
  AttacherType = Attacher::AttachEngine3D
  Height = 10
  Length = 2
  Placement = pos=(-55,-6,24.5) rot=(0,0,1;0rad)
  Width = 3
FEATURE [Part::Box] Box047  label="Cube046"
  AttacherType = Attacher::AttachEngine3D
  Height = 10
  Length = 2
  Placement = pos=(-72,-14,24.5) rot=(0,0,1;0rad)
  Width = 3
FEATURE [Part::Box] Box048  label="Cube047"
  AttacherType = Attacher::AttachEngine3D
  Height = 10
  Length = 2
  Placement = pos=(-72,-6,24.5) rot=(0,0,1;0rad)
  Width = 3
FEATURE [Part::Box] Box049  label="Cube048"
  AttacherType = Attacher::AttachEngine3D
  Height = 10
  Length = 2
  Placement = pos=(-55,-14,24.5) rot=(0,0,1;0rad)
  Width = 3
FEATURE [Part::MultiFuse] Fusion006002011004053036004001028003005014008
  Placement = pos=(0,-9,0) rot=(0,0,1;0rad)
  Shapes = -> [Box046,Box048,Box047,Box049]
FEATURE [Part::Box] Box050  label="Cube049"
  AttacherType = Attacher::AttachEngine3D
  Height = 5
  Length = 6
  Placement = pos=(-74,-16,24.5) rot=(0,0,1;0rad)
  Width = 15
FEATURE [Part::Box] Box053  label="Cube052"
  AttacherType = Attacher::AttachEngine3D
  Height = 5
  Length = 6
  Placement = pos=(-57,-16,24.5) rot=(0,0,1;0rad)
  Width = 15
FEATURE [Part::MultiFuse] Fusion006002011004053036004001028003005014009
  Shapes = -> [Box050,Box053]
FEATURE [Part::Fillet] Fillet001028
  Base = -> Fusion006002011004053036004001028003005014009
  Edges = 8 edges r=1: [Edge1,Edge3,Edge5,Edge7,Edge13,Edge15,Edge17,Edge19]
  Placement = pos=(0,-9,0) rot=(0,0,1;0rad)
FEATURE [Part::Cylinder] Cylinder010
  Angle = 360
  AttacherType = Attacher::AttachEngine3D
  Height = 36
  Placement = pos=(-65,105,0) rot=(0,0,1;0rad)
  Radius = 1.9
FEATURE [Part::Cylinder] Cylinder011
  Angle = 360
  AttacherType = Attacher::AttachEngine3D
  Height = 36
  Placement = pos=(65,105,0) rot=(0,0,1;0rad)
  Radius = 1.9
FEATURE [Part::Feature] Cut002015019
  Placement = pos=(65,105,27.5) rot=(0,1,0;3.14159rad)
  shape: bbox 20 x 20 x 3 mm, 23 faces (baked)
FEATURE [Part::Feature] Cut002015020
  Placement = pos=(-65,105,27.5) rot=(0,1,0;3.14159rad)
  shape: bbox 20 x 20 x 3 mm, 23 faces (baked)
FEATURE [Part::MultiFuse] Fusion006002011004053036004001028003005014014
  Shapes = -> [Cut002015019,Cut002015004,Cut002015007,Cut002015003,Cut002015005,Cut002015006,Cut002015002,Cut002015020]
FEATURE [Part::Cylinder] Cylinder014
  Angle = 360
  AttacherType = Attacher::AttachEngine3D
  Height = 10
  Placement = pos=(-73,45,21) rot=(0,0,1;0rad)
  Radius = 1.9
FEATURE [Part::Cylinder] Cylinder015
  Angle = 360
  AttacherType = Attacher::AttachEngine3D
  Height = 10
  Placement = pos=(-73,-125,21) rot=(0,0,1;0rad)
  Radius = 1.9
FEATURE [Part::Cylinder] Cylinder016
  Angle = 360
  AttacherType = Attacher::AttachEngine3D
  Height = 10
  Placement = pos=(73,-40,21) rot=(0,0,1;0rad)
  Radius = 1.9
FEATURE [Part::Cylinder] Cylinder017
  Angle = 360
  AttacherType = Attacher::AttachEngine3D
  Height = 10
  Placement = pos=(73,10,21) rot=(0,0,1;0rad)
  Radius = 1.9
FEATURE [Part::Cylinder] Cylinder018
  Angle = 360
  AttacherType = Attacher::AttachEngine3D
  Height = 10
  Placement = pos=(-73,95,21) rot=(0,0,1;0rad)
  Radius = 1.9
FEATURE [Part::Cylinder] Cylinder019
  Angle = 360
  AttacherType = Attacher::AttachEngine3D
  Height = 10
  Placement = pos=(-73,-75,21) rot=(0,0,1;0rad)
  Radius = 1.9
FEATURE [Part::Chamfer] Chamfer005007002021
  Base = -> Cut002015011
  Edges = 1 edges r=0.99: [Edge36]
FEATURE [Part::Chamfer] Chamfer005007002022
  Base = -> Cut002006
  Edges = 1 edges r=0.99: [Edge56]
FEATURE [Part::Chamfer] Chamfer005007002023
  Base = -> Cut002015015
  Edges = 1 edges r=0.99: [Edge40]
FEATURE [Part::Chamfer] Chamfer005007002024
  Base = -> Cut002004
  Edges = 1 edges r=0.99: [Edge27]
FEATURE [Part::Chamfer] Chamfer005007002025
  Base = -> Cut002015010
  Edges = 1 edges r=0.99: [Edge41]
FEATURE [Part::Chamfer] Chamfer005007002026
  Base = -> Cut002015013
  Edges = 1 edges r=0.99: [Edge78]
FEATURE [Part::MultiFuse] Fusion006002011004053036004001028003005014018003
  Shapes = -> [Fillet001028,Cut002015017]
FEATURE [Part::MultiFuse] Fusion006002011004053036004001028003005014018004
  Shapes = -> [Fillet001025,Fusion006002011004053036004001028003005014008]
FEATURE [Part::MultiFuse] Fusion006002011004053036004001028003005014018002
  Placement = pos=(0,0,3) rot=(0,0,1;0rad)
  Shapes = -> [Cylinder019,Cylinder014,Cylinder015,Cylinder016,Cylinder017,Cylinder018]
FEATURE [Part::MultiFuse] Fusion006002011004053036004001028003005012
  Shapes = -> [Cylinder008,Cylinder005,Cylinder006,Cylinder003,Cylinder004,Cylinder007]
FEATURE [Part::MultiFuse] Fusion006002011004053036004001028003005014016
  Shapes = -> [Cylinder010,Cylinder011]
FEATURE [Part::MultiFuse] Fusion006002011004053036004001028003005014017
  Shapes = -> [Fusion006002011004053036004001028003005012,Fusion006002011004053036004001028003005014016]
FEATURE [Part::MultiFuse] Fusion006002011004053036004001028003005014018007
  Shapes = -> [Chamfer005007002017,Chamfer001001,Chamfer005007002003,Chamfer005007002005,Chamfer005007002006,Chamfer005007002008,Chamfer005007002009,Chamfer005007002010,Chamfer005007002011,Chamfer005007002012,Chamfer005007002013,Chamfer005007002014,Chamfer005007002015]
FEATURE [Part::Box] Box056  label="Cube055"
  AttacherType = Attacher::AttachEngine3D
  Height = 10
  Length = 2
  Placement = pos=(-80.5,-141,21.5) rot=(0,0,1;0rad)
  Width = 8
FEATURE [Part::Box] Box057  label="Cube056"
  AttacherType = Attacher::AttachEngine3D
  Height = 10
  Length = 2
  Placement = pos=(-80.5,-56,21.5) rot=(0,0,1;0rad)
  Width = 8
FEATURE [Part::Box] Box058  label="Cube057"
  AttacherType = Attacher::AttachEngine3D
  Height = 10
  Length = 2
  Placement = pos=(-80.5,29,21.5) rot=(0,0,1;0rad)
  Width = 8
FEATURE [Part::Box] Box059  label="Cube058"
  AttacherType = Attacher::AttachEngine3D
  Height = 10
  Length = 2
  Placement = pos=(-80.5,114,21.5) rot=(0,0,1;0rad)
  Width = 8
FEATURE [Part::MultiFuse] Fusion006002011004053036004001028003005014018010
  Shapes = -> [Box056,Box057,Box058,Box059]
FEATURE [Part::Box] Box060  label="Cube059"
  AttacherType = Attacher::AttachEngine3D
  Height = 10
  Length = 2
  Placement = pos=(78.5,-55.5,21.5) rot=(0,0,1;0rad)
  Width = 8
FEATURE [Part::Box] Box061  label="Cube060"
  AttacherType = Attacher::AttachEngine3D
  Height = 10
  Length = 2
  Placement = pos=(78.5,29.5,21.5) rot=(0,0,1;0rad)
  Width = 8
FEATURE [Part::MultiFuse] Fusion006002011004053036004001028003005014018011
  Shapes = -> [Box060,Box061]
FEATURE [Part::MultiFuse] Fusion006002011004053036004001028003005014018012  label="side-bolt-cut"
  Placement = pos=(0,-1,0) rot=(0,0,1;0rad)
  Shapes = -> [Fusion006002011004053036004001028003005014018010,Fusion006002011004053036004001028003005014018011]
FEATURE [Part::MultiFuse] Fusion006002011004053036004001028003005014018013
  Shapes = -> [Fusion001010002032014,Fusion001010002032002,Fusion001010002032003,Fusion001010002032004,Fusion001010002032005,Fusion001010002032006,Fusion001010002032007,Fusion001010002032008,Fusion001010002032009,Fusion001010002032010,Fusion001010002032011,Fusion001010002032012]
FEATURE [Part::MultiFuse] Fusion006002011004053036004001028003005014018017
  Shapes = -> [Fusion001010002017,Fusion001010002016,Fusion001010002015]
FEATURE [Part::MultiFuse] Fusion001010002022
  Shapes = -> [Cut002001,Cut002]
FEATURE [Part::Cut] Cut002015026002
  Base = -> Fusion001010002022
  Tool = -> Fusion006002011004053036004001028003005014018017
FEATURE [Part::Box] Box062  label="Cube061"
  AttacherType = Attacher::AttachEngine3D
  Height = 33
  Length = 10
  Placement = pos=(-88.5,-145,2.5) rot=(0,0,1;0rad)
  Width = 18
FEATURE [Part::Cut] Cut002015026003
  Base = -> Cut002015026002
  Tool = -> Box062
FEATURE [Part::Chamfer] Chamfer005007002029
  Base = -> Cut002015026003
  Edges = 1 edges r=0.99: [Edge82]
FEATURE [Part::Cut] Cut002015026004
  Base = -> Cut002013
  Tool = -> Fusion006002011004053036004001028003005014018012
FEATURE [Part::Chamfer] Chamfer005007002030
  Base = -> Cut002015026004
  Edges = 50 edges r=0.4: [Edge4,Edge7,Edge9,Edge58,Edge59,Edge60,Edge61,Edge62,Edge63,Edge64,Edge65,Edge66,Edge67,Edge68,Edge69,Edge70,Edge71,Edge72,Edge73,Edge74,Edge75,Edge76,Edge77,Edge78,Edge79,Edge80,Edge81,Edge82,Edge83,Edge84,Edge85,Edge86,Edge87,Edge88,Edge89,Edge90,Edge91,Edge92,Edge93,Edge94,Edge95,Edge96,Edge97,+7 more]
FEATURE [Part::Cut] Cut002015026005
  Base = -> Chamfer005007002030
  Tool = -> Cut002012
FEATURE [Part::Cut] Cut002015026006
  Base = -> Cut002015026005
  Tool = -> Fusion006002011004053036004001028003005014018013
FEATURE [Part::Cut] Cut002015026007
  Base = -> Cut002015026006
  Tool = -> Fusion006002011004053036004001028003005014018002
FEATURE [Part::MultiFuse] Fusion006002011004053036004001028003005014018018
  Shapes = -> [Cut002015026007,Fusion006002011004053036004001028003005014018003]
FEATURE [Part::Cut] Cut002015026008
  Base = -> Fusion006002011004053036004001028003005014018018
  Tool = -> Fusion006002011004053036004001028003005014018004
FEATURE [Part::MultiFuse] Fusion006002011004053036004001028003005014018019
  Shapes = -> [Cut002015026008,Fusion006002011004053036004001028003005014018007]
FEATURE [Part::MultiFuse] Fusion006002011004053036004001028003005014018020
  Shapes = -> [Fusion006002011004053036004001028003005014018019,Fusion006002011004053036004001028003005014014]
FEATURE [Part::Cut] Cut002015026009
  Base = -> Fusion006002011004053036004001028003005014018020
  Tool = -> Fusion006002011004053036004001028003005014017
FEATURE [Part::Refine] Cut002015026009001
  Source = -> Cut002015026009
FEATURE [Part::Chamfer] Chamfer005007002031
  Base = -> Cut002015026009001
  Edges = 24 edges r=1: [Edge333,Edge334,Edge335,Edge336,Edge337,Edge338,Edge339,Edge340,Edge1259,Edge1275,Edge1281,Edge1285,Edge1564,Edge3928,Edge3960,Edge3972,Edge3980,Edge3981,Edge3982,Edge3983,Edge3984,Edge3985,Edge3986,Edge3987]
FEATURE [Part::Feature] Chamfer005007002031001
  shape: bbox 280 x 279 x 8.5 mm, 1486 faces (baked)
